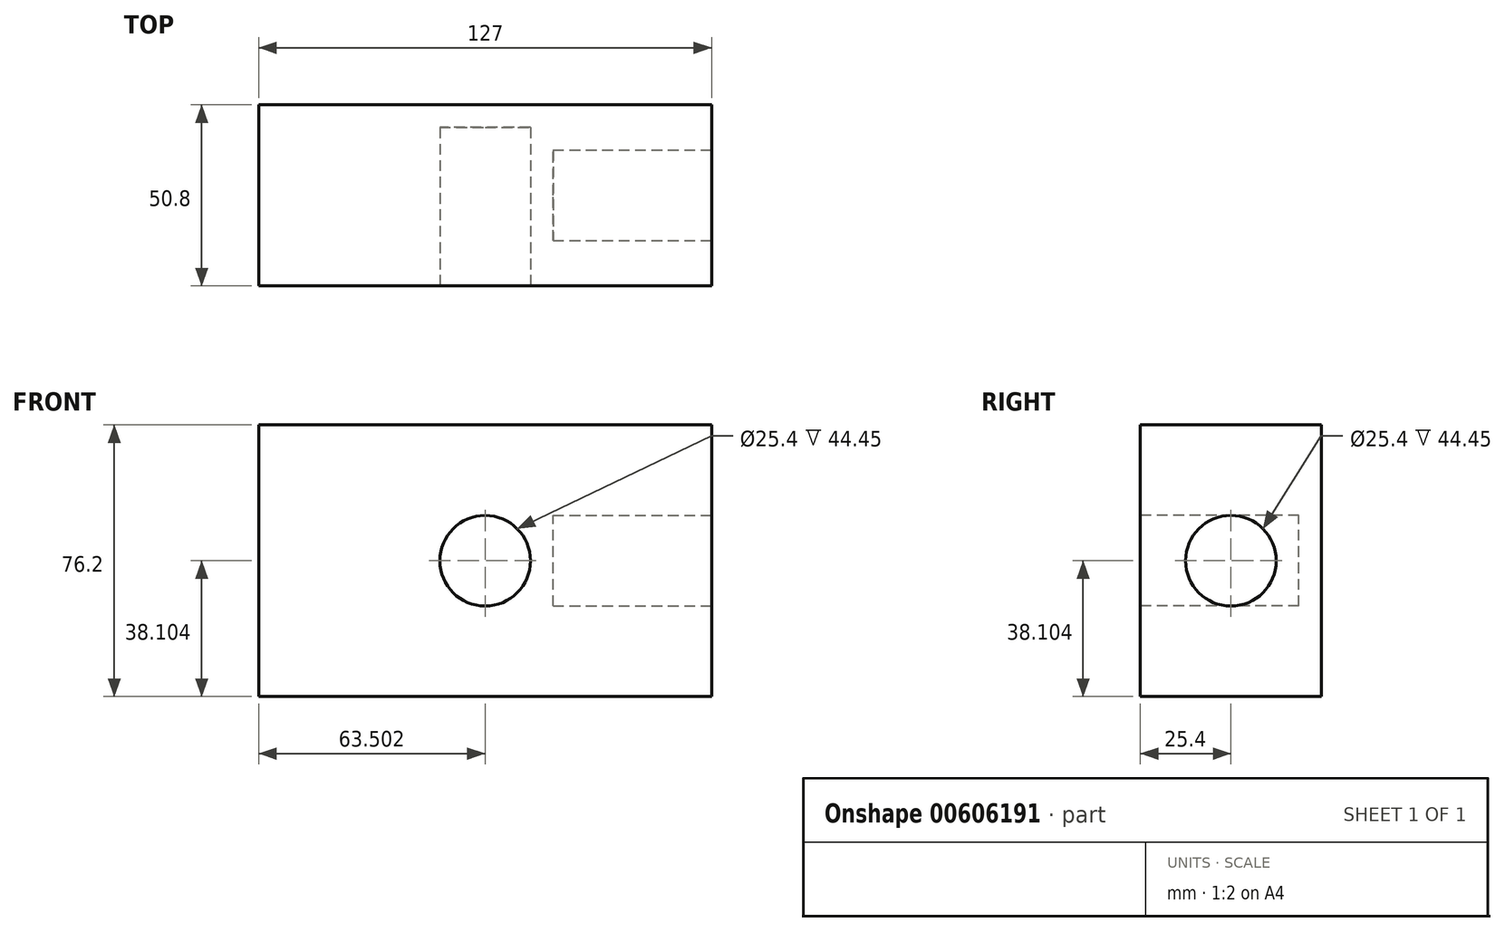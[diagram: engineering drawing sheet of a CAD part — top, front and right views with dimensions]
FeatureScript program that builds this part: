
annotation { "Feature Type Name" : "Feature", "Feature Type Description" : "" }
export const myFeature = defineFeature(function(context is Context, id is Id, definition is map)
    precondition{}
    {
        {
            var Q0;
            Q0=qCreatedBy(makeId("Front.planeOp"),FACE);
            var sketch = newSketch(context, id + "F0", { "sketchPlane" : qUnion([Q0])});
            skLineSegment(sketch, "E0.bottom", {"start": v(-62.28, 11.3) * mm, "end": v(64.72, 11.3) * mm});
            skLineSegment(sketch, "E0.top", {"start": v(-62.28, -64.9) * mm, "end": v(64.72, -64.9) * mm});
            skLineSegment(sketch, "E0.left", {"start": v(-62.28, 11.3) * mm, "end": v(-62.28, -64.9) * mm});
            skLineSegment(sketch, "E0.right", {"start": v(64.72, 11.3) * mm, "end": v(64.72, -64.9) * mm});
            skSolve(sketch);
        }
        {
            var Q0;
            Q0=makeQuery(id+"F0.imprint","IMPRINT",FACE,{"disambiguationData":[TD([[makeQuery(id+"F0.imprint","IMPRINT",EDGE,{"derivedFrom":sQuery(id+"F0.wireOp",EDGE,"E0.bottom")}),-1.0]])]});
            extrude(context, id + "F1", {"entities" : qUnion([Q0]), "depth" : 25.4 * mm, "offsetDistance" : 25.4 * mm, "hasSecondDirection" : true, "secondDirectionOppositeDirection" : true, "secondDirectionDepth" : 25.4 * mm});
        }
        {
            var Q0;
            Q0=makeQuery(id+"F1.opExtrude","CAP_FACE",FACE,{"disambiguationData":[OSD([sQuery(id+"F0.wireOp",EDGE,"E0.bottom"),sQuery(id+"F0.wireOp",EDGE,"E0.top"),sQuery(id+"F0.wireOp",EDGE,"E0.left"),sQuery(id+"F0.wireOp",EDGE,"E0.right")])],"isStart":false});
            var sketch = newSketch(context, id + "F2", { "sketchPlane" : qUnion([Q0])});
            skCircle(sketch, "E1", {"center": v(1.22, -26.8) * mm, "radius": 12.7 * mm});
            skSolve(sketch);
        }
        {
            var Q0;
            Q0=makeQuery(id+"F2.imprint","IMPRINT",FACE,{"disambiguationData":[TD([[makeQuery(id+"F2.imprint","IMPRINT",EDGE,{"derivedFrom":sQuery(id+"F2.wireOp",EDGE,"E1")}),1.0]])]});
            var Q1;
            Q1 = qSketchRegion(id + "F4", true);
            extrude(context, id + "F3", {"entities" : qUnion([Q0, Q1]), "operationType" : NewBodyOperationType.REMOVE, "oppositeDirection" : true, "depth" : 44.45 * mm, "offsetDistance" : 25.4 * mm});
        }
        {
            var Q0;
            Q0=makeQuery(id+"F1.opExtrude","SWEPT_FACE",FACE,{"disambiguationData":[OSD([sQuery(id+"F0.wireOp",EDGE,"E0.right")])]});
            var sketch = newSketch(context, id + "F4", { "sketchPlane" : qUnion([Q0])});
            skCircle(sketch, "E2", {"center": v(0, -26.8) * mm, "radius": 12.7 * mm});
            skPoint(sketch, "E2.centerSnap0", {"position": v(25.4, -26.8) * mm});
            skSolve(sketch);
        }
        {
            var Q0;
            Q0=makeQuery(id+"F4.imprint","IMPRINT",FACE,{"disambiguationData":[TD([[makeQuery(id+"F4.imprint","IMPRINT",EDGE,{"derivedFrom":sQuery(id+"F4.wireOp",EDGE,"E2")}),1.0]])]});
            extrude(context, id + "F5", {"entities" : qUnion([Q0]), "operationType" : NewBodyOperationType.REMOVE, "oppositeDirection" : true, "depth" : 44.45 * mm, "offsetDistance" : 25.4 * mm});
        }
    });
